# Revit family: Sanitary_Wash-Basins_HIMACS_HIMACS-Bowl-CB-6033
name_source: partatom
category: Plumbing Fixtures
revit_build: Autodesk Revit 2018 (Build: 20190510_1515(x64)
units: mm (PartAtom-declared; Revit-internal decimal feet)

## family parameters
Cut with Voids When Loaded = No
Host = Face
OmniClass Number = 23.31.13.11
OmniClass Title = Single Sinks
Part Type = Normal
Room Calculation Point = No
Round Connector Dimension = Use Diameter
Shared = No

## types (2) — shared parameters
BIMobject category = Wash Basins
Default Elevation = 1219 mm
Description = HIMACS Bowls offer superb ease of cleaning and a warm and pleasant feel, making them the ideal solution for creating the bathroom of your dreams. They are manufactured using a casting process and ideally suited for both flush mounting and installation into a bathroom vanity top.

Available in Alpine White S028.

Without overflow. Under Mounted.

HIMACS is a solid surface material that can be moulded into any shape. It is widely used for architectural and interior applications, such as sculptural and high performance wall-cladding or kitchen, bathroom and furniture surfaces, in commercial, residential and public space projects. It is composed of acrylic, natural minerals and pigments that come together to provide a smooth, non-porous and visually seamless surface which meets the highest standards for quality, aesthetics, fabrication, functionality and hygiene – offering manifold advantages over conventional materials.

Visit himacs.eu for more information.
Design country = Spain
Diameter = 45 mm  [stored 0.147638 ft]
Edition number = 1
IFC Classification = Furnishing Element
Main material = HIMACS - Ceramic -  Alpine White
Manufacturer = HIMACS
Manufacturer country = Spain
Manufacturer name = HIMACS
Material main = Solid surface
Material secondary = Natural Acrylic Stone
Model = HIMACS Bowl CB 6033
NBS Reference Code = 35-65-70-94
NBS Reference Description = Wash Basin Systems
Product Guid = eedae098-795c-4f03-83b5-a55a429772f6
Product SKU = CB6033
Product certification = http://himacs.eu
Product data url = https://bimobject.com
Product family = Sinks, Baby Baths & Bowls
Product group = Bowls
Product name = HIMACS Bowl CB 6033
QR code = https://bimobject.com
UNSPSC Code = 301815
URL = https://himacs.eu
Uniclass 1.4 Code = L7212
Uniclass 1.4 Description = Washbasins
Uniclass 2.0 Code = SS-35-65-70-94
Uniclass 2.0 Description = Wash Basin Systems
Weight Net (Kg) = 7,5

## per-type parameters (varying)
| type | Overflow - (With) | Overflow - (Without) |
| HIMACS Bowl CB 6033 with Overflow | Yes | No |
| HIMACS Bowl CB 6033 without Overflow | No | Yes |

note: [stored X ft] marks values corroborated as IEEE doubles in the binary element streams (Revit-internal decimal feet)

## geometry (parser evidence)
native form markers: Sweep x3
no freeform markers — native parametric forms only
